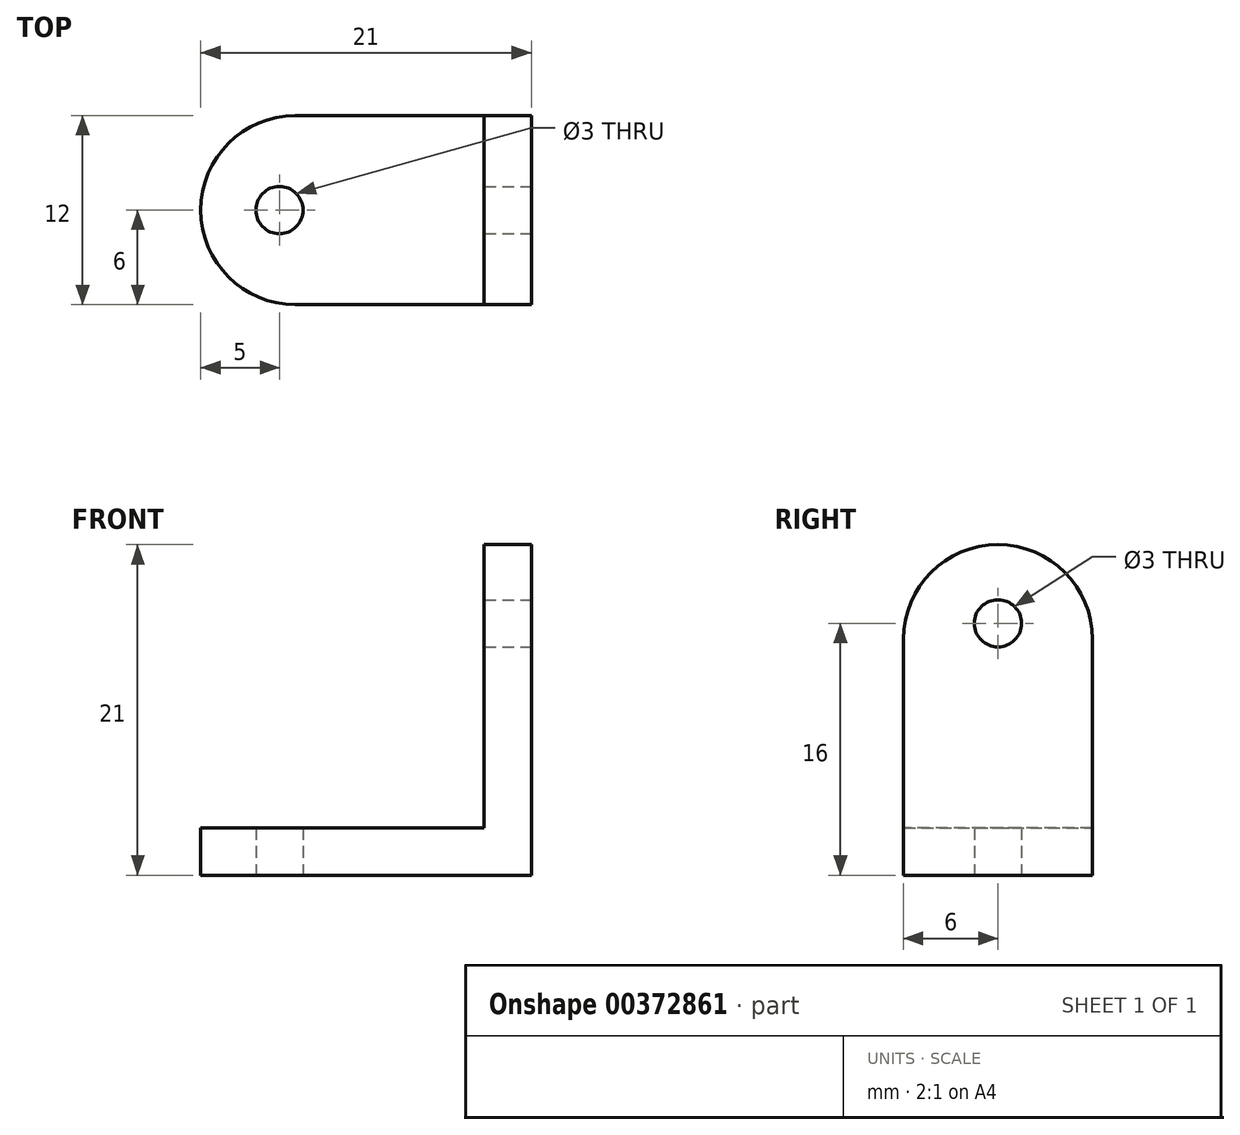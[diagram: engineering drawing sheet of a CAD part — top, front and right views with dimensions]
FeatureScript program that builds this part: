
annotation { "Feature Type Name" : "Feature", "Feature Type Description" : "" }
export const myFeature = defineFeature(function(context is Context, id is Id, definition is map)
    precondition{}
    {
        {
            var Q0;
            Q0=qCreatedBy(makeId("Top.planeOp"),FACE);
            var sketch = newSketch(context, id + "F0", { "sketchPlane" : qUnion([Q0])});
            skLineSegment(sketch, "E0.bottom", {"start": v(-15, 0) * mm, "end": v(0, 0) * mm});
            skLineSegment(sketch, "E0.top", {"start": v(-15, -12) * mm, "end": v(0, -12) * mm});
            skLineSegment(sketch, "E0.right", {"start": v(0, 0) * mm, "end": v(0, -12) * mm});
            skArc(sketch, "E1", {"start": v(-15, 0) * mm, "mid": v(-21, -6) * mm, "end": v(-15, -12) * mm});
            skCircle(sketch, "E2", {"center": v(-16, -6) * mm, "radius": 1.5 * mm});
            skSolve(sketch);
        }
        {
            var Q0;
            Q0=qCreatedBy(makeId("Right.planeOp"),FACE);
            var sketch = newSketch(context, id + "F1", { "sketchPlane" : qUnion([Q0])});
            skLineSegment(sketch, "E3.top", {"start": v(0, 0) * mm, "end": v(-12, 0) * mm});
            skLineSegment(sketch, "E3.left", {"start": v(0, 15) * mm, "end": v(0, 0) * mm});
            skLineSegment(sketch, "E3.right", {"start": v(-12, 15) * mm, "end": v(-12, 0) * mm});
            skArc(sketch, "E4", {"start": v(0, 15) * mm, "mid": v(-6, 21) * mm, "end": v(-12, 15) * mm});
            skCircle(sketch, "E5", {"center": v(-6, 16) * mm, "radius": 1.5 * mm});
            skSolve(sketch);
        }
        {
            var Q0;
            Q0=makeQuery(id+"F0.imprint","IMPRINT",FACE,{"disambiguationData":[TD([[makeQuery(id+"F0.imprint","IMPRINT",EDGE,{"derivedFrom":sQuery(id+"F0.wireOp",EDGE,"E0.bottom")}),-1.0]])]});
            extrude(context, id + "F2", {"entities" : qUnion([Q0]), "depth" : 3 * mm});
        }
        {
            var Q0;
            Q0=makeQuery(id+"F1.imprint","IMPRINT",FACE,{"disambiguationData":[TD([[makeQuery(id+"F1.imprint","IMPRINT",EDGE,{"derivedFrom":sQuery(id+"F1.wireOp",EDGE,"E3.top")}),-1.0]])]});
            extrude(context, id + "F3", {"entities" : qUnion([Q0]), "operationType" : NewBodyOperationType.ADD, "oppositeDirection" : true, "depth" : 3 * mm});
        }
    });
